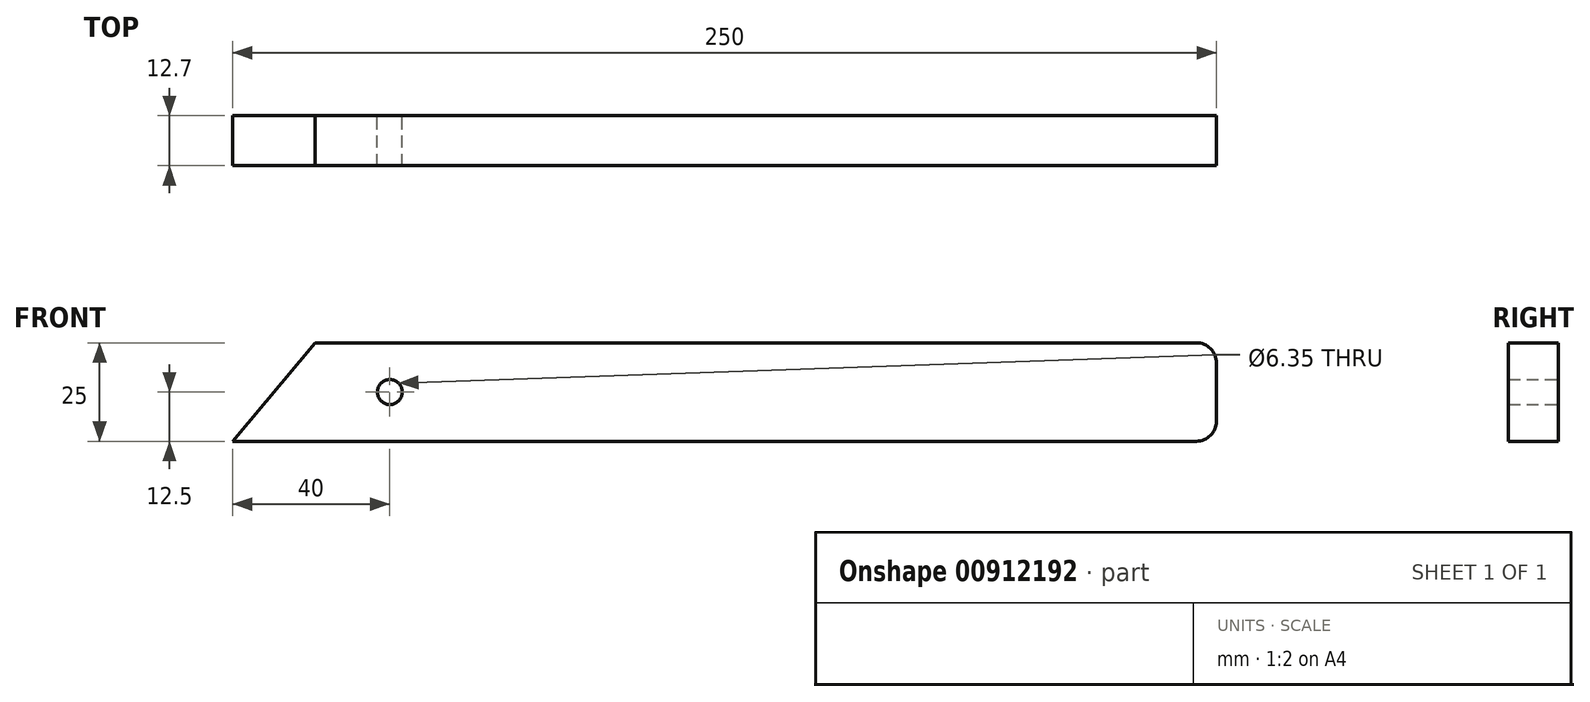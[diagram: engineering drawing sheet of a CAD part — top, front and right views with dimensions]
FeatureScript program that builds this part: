
annotation { "Feature Type Name" : "Feature", "Feature Type Description" : "" }
export const myFeature = defineFeature(function(context is Context, id is Id, definition is map)
    precondition{}
    {
        {
            var Q0;
            Q0=qCreatedBy(makeId("Front.planeOp"),FACE);
            var sketch = newSketch(context, id + "F0", { "sketchPlane" : qUnion([Q0])});
            skLineSegment(sketch, "E0.bottom", {"start": v(0, 0) * mm, "end": v(250, 0) * mm});
            skLineSegment(sketch, "E0.top", {"start": v(0, 25) * mm, "end": v(250, 25) * mm});
            skLineSegment(sketch, "E0.left", {"start": v(0, 0) * mm, "end": v(0, 25) * mm});
            skLineSegment(sketch, "E0.right", {"start": v(250, 0) * mm, "end": v(250, 25) * mm});
            skLineSegment(sketch, "E1", {"start": v(0, 0) * mm, "end": v(20.98, 25) * mm});
            skCircle(sketch, "E2", {"center": v(40, 12.5) * mm, "radius": 3.18 * mm});
            skPoint(sketch, "E2.centerSnap0", {"position": v(0, 12.5) * mm});
            skSolve(sketch);
        }
        {
            var Q0;
            Q0=makeQuery(id+"F0.imprint","IMPRINT",FACE,{"disambiguationData":[TD([[makeQuery(id+"F0.imprint","IMPRINT",EDGE,{"derivedFrom":sQuery(id+"F0.wireOp",EDGE,"E0.bottom")}),1.0]])]});
            extrude(context, id + "F1", {"entities" : qUnion([Q0]), "depth" : 12.7 * mm, "offsetDistance" : 25.4 * mm});
        }
        {
            var Q0;
            Q0=makeQuery(id+"F1.opExtrude","SWEPT_EDGE",EDGE,{"disambiguationData":[OSD([sQuery(id+"F0.wireOp",EDGE,"E0.top"),sQuery(id+"F0.wireOp",EDGE,"E0.right")])]});
            fillet(context, id + "F2", {"entities" : qUnion([Q0]), "radius" : 5.08 * mm, "tangentPropagation" : true, "allowEdgeOverflow" : false});
        }
        {
            var Q0;
            Q0=makeQuery(id+"F1.opExtrude","SWEPT_EDGE",EDGE,{"disambiguationData":[OSD([sQuery(id+"F0.wireOp",EDGE,"E0.bottom"),sQuery(id+"F0.wireOp",EDGE,"E0.right")])]});
            fillet(context, id + "F3", {"entities" : qUnion([Q0]), "radius" : 5.08 * mm, "tangentPropagation" : true, "allowEdgeOverflow" : false});
        }
    });
